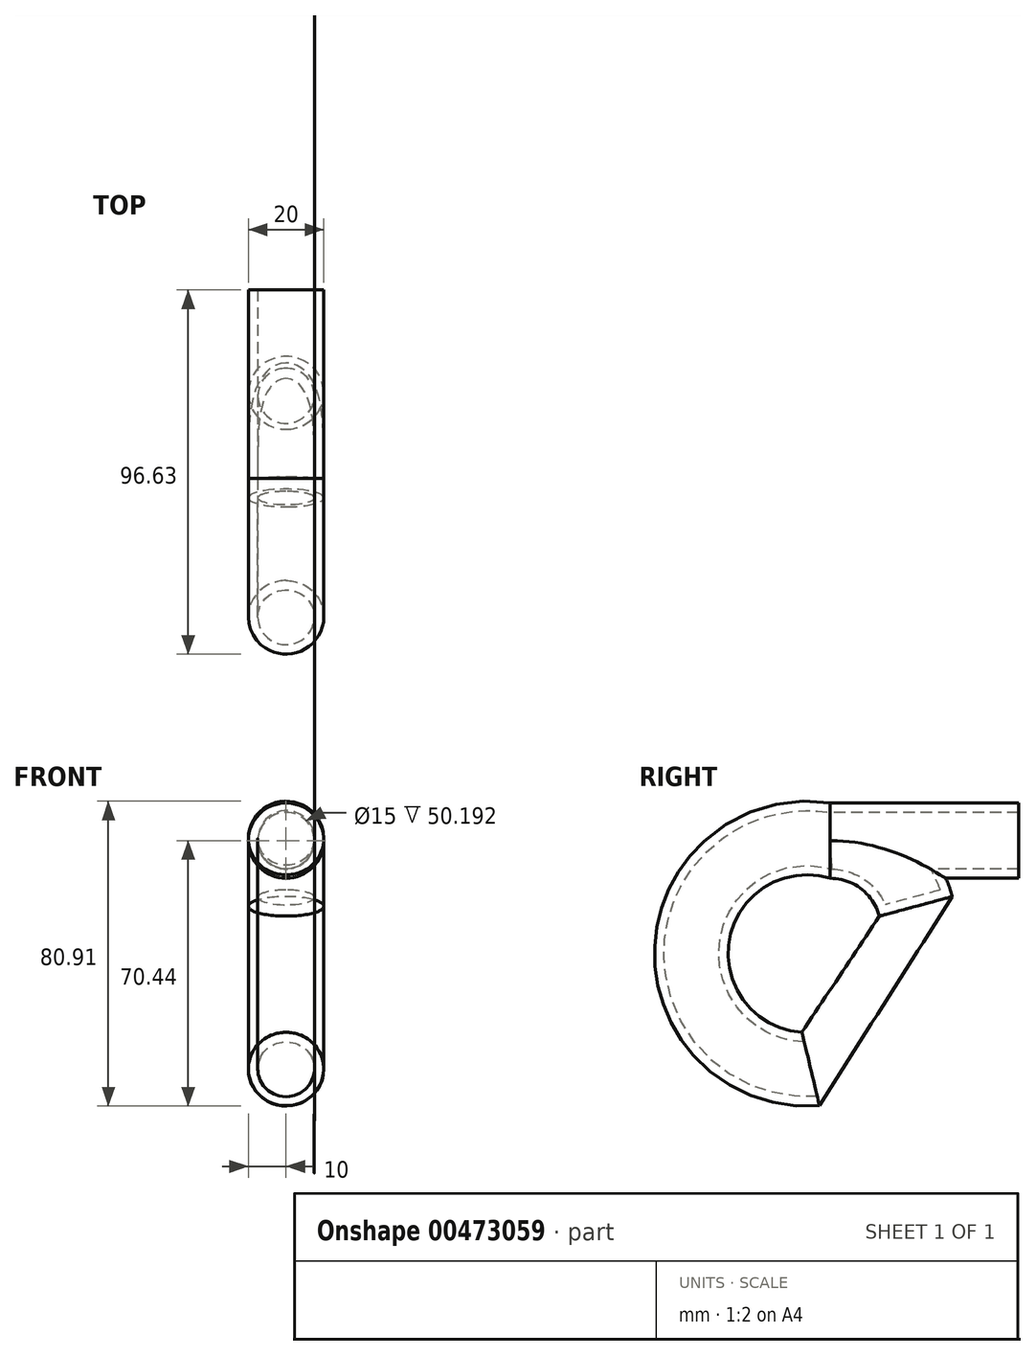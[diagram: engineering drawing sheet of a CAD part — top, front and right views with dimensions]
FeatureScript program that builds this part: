
annotation { "Feature Type Name" : "Feature", "Feature Type Description" : "" }
export const myFeature = defineFeature(function(context is Context, id is Id, definition is map)
    precondition{}
    {
        {
            var Q0;
            Q0=qCreatedBy(makeId("Front.planeOp"),FACE);
            var sketch = newSketch(context, id + "F0", { "sketchPlane" : qUnion([Q0])});
            skCircle(sketch, "E0", {"center": v(0, 0) * mm, "radius": 10 * mm});
            skPoint(sketch, "E0.first.point", {"position": v(8.63, 5.06) * mm});
            skPoint(sketch, "E0.second.point", {"position": v(8.9, 4.56) * mm});
            skPoint(sketch, "E0.third.point", {"position": v(8.05, 5.94) * mm});
            skLineSegment(sketch, "E1", {"start": v(0, -23.51) * mm, "end": v(33.54, -23.51) * mm});
            skSolve(sketch);
        }
        {
            var Q0;
            Q0=makeQuery(id+"F0.imprint","IMPRINT",FACE,{"disambiguationData":[TD([[makeQuery(id+"F0.imprint","IMPRINT",EDGE,{"derivedFrom":sQuery(id+"F0.wireOp",EDGE,"E0")}),1.0]])]});
            var Q1;
            Q1=sQuery(id+"F0.wireOp",EDGE,"E1");
            revolve(context, id + "F1", {"entities" : qUnion([Q0]), "axis" : qUnion([Q1]), "revolveType" : RevolveType.ONE_DIRECTION, "oppositeDirection" : true, "angle" : 75 * degree});
        }
        {
            var Q0;
            Q0=makeQuery(id+"F0.imprint","IMPRINT",FACE,{"disambiguationData":[TD([[makeQuery(id+"F0.imprint","IMPRINT",EDGE,{"derivedFrom":sQuery(id+"F0.wireOp",EDGE,"E0")}),1.0]])]});
            extrude(context, id + "F2", {"entities" : qUnion([Q0]), "oppositeDirection" : true, "depth" : 50 * mm});
        }
        {
            var Q0;
            Q0=qCreatedBy(makeId("Right.planeOp"),FACE);
            var sketch = newSketch(context, id + "F3", { "sketchPlane" : qUnion([Q0])});
            skArc(sketch, "E2", {"start": v(0, 0) * mm, "mid": v(-36.67, -27.37) * mm, "end": v(-5.18, -60.57) * mm});
            skSolve(sketch);
        }
        {
            var Q0;
            Q0=makeQuery(id+"F0.imprint","IMPRINT",FACE,{"disambiguationData":[TD([[makeQuery(id+"F0.imprint","IMPRINT",EDGE,{"derivedFrom":sQuery(id+"F0.wireOp",EDGE,"E0")}),1.0]])]});
            var Q1;
            Q1=sQuery(id+"F3.wireOp",EDGE,"E2");
            sweep(context, id + "F4", {"operationType" : NewBodyOperationType.ADD, "profiles" : qUnion([Q0]), "path" : qUnion([Q1])});
        }
        {
            var Q0;
            Q0=makeQuery(id+"F1.opRevolve","CAP_FACE",FACE,{"disambiguationData":[OSD([sQuery(id+"F0.wireOp",EDGE,"E0")])],"isStart":false});
            var Q1;
            Q1=makeQuery(id+"F4.opSweep","CAP_FACE",FACE,{"disambiguationData":[OSD([sQuery(id+"F0.wireOp",EDGE,"E0"),sQuery(id+"F3.wireOp",VERTEX,"E2.end")])],"isStart":false});
            loft(context, id + "F5", {"sheetProfilesArray" : [{ "sheetProfileEntities" : qUnion([Q0]) }, { "sheetProfileEntities" : qUnion([Q1]) }]});
        }
        {
            var Q0;
            Q0=makeQuery(id+"F2.opExtrude","CAP_FACE",FACE,{"disambiguationData":[OSD([sQuery(id+"F0.wireOp",EDGE,"E0")])],"isStart":false});
            var Q1;
            Q1=makeQuery(id+"F4.opSweep","CAP_FACE",FACE,{"disambiguationData":[OSD([sQuery(id+"F0.wireOp",EDGE,"E0"),sQuery(id+"F3.wireOp",VERTEX,"E2.end")])],"isStart":false});
            shell(context, id + "F6", {"entities" : qUnion([Q0, Q1]), "thickness" : 2.5 * mm});
        }
        {
            var Q0;
            Q0=sQuery(id+"F0.wireOp",VERTEX,"E0.center");
            var Q1;
            Q1=makeQuery(id+"F2.opExtrude","SWEPT_BODY",BODY,{"disambiguationData":[OSD([sQuery(id+"F0.wireOp",EDGE,"E0")])]});
            var Q2;
            Q2=makeQuery(id+"F1.opRevolve","SWEPT_BODY",BODY,{"disambiguationData":[OSD([sQuery(id+"F0.wireOp",EDGE,"E0")])]});
            hole(context, id + "F7", {"style" : HoleStyle.SIMPLE, "endStyle" : HoleEndStyle.THROUGH, "holeDiameter" : 15 * mm, "isTappedThrough" : true, "tappedDepth" : 12 * mm, "tapClearance" : 3, "locations" : qUnion([Q0]), "scope" : qUnion([Q1, Q2])});
        }
    });
